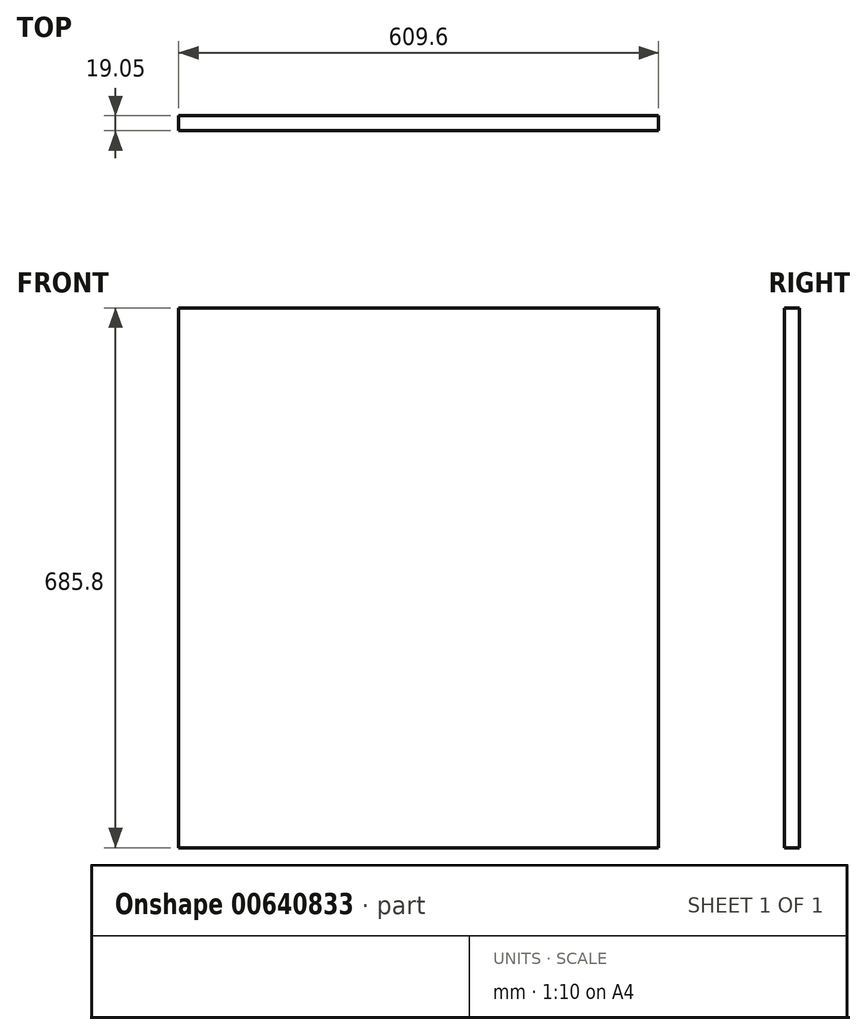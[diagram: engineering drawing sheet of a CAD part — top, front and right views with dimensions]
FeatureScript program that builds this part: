
annotation { "Feature Type Name" : "Feature", "Feature Type Description" : "" }
export const myFeature = defineFeature(function(context is Context, id is Id, definition is map)
    precondition{}
    {
        {
            var Q0;
            Q0=qCreatedBy(makeId("Front.planeOp"),FACE);
            var sketch = newSketch(context, id + "F0", { "sketchPlane" : qUnion([Q0])});
            skLineSegment(sketch, "E0.bottom", {"start": v(-304.8, 342.9) * mm, "end": v(304.8, 342.9) * mm});
            skLineSegment(sketch, "E0.top", {"start": v(-304.8, -342.9) * mm, "end": v(304.8, -342.9) * mm});
            skLineSegment(sketch, "E0.left", {"start": v(-304.8, 342.9) * mm, "end": v(-304.8, -342.9) * mm});
            skLineSegment(sketch, "E0.right", {"start": v(304.8, 342.9) * mm, "end": v(304.8, -342.9) * mm});
            skPoint(sketch, "E0.middle", {"position": v(0, 0) * mm});
            skSolve(sketch);
        }
        {
            var Q0;
            Q0=makeQuery(id+"F0.imprint","IMPRINT",FACE,{"disambiguationData":[TD([[makeQuery(id+"F0.imprint","IMPRINT",EDGE,{"derivedFrom":sQuery(id+"F0.wireOp",EDGE,"E0.bottom")}),-1.0]])]});
            extrude(context, id + "F1", {"entities" : qUnion([Q0]), "depth" : 19.05 * mm, "offsetDistance" : 25.4 * mm});
        }
    });
